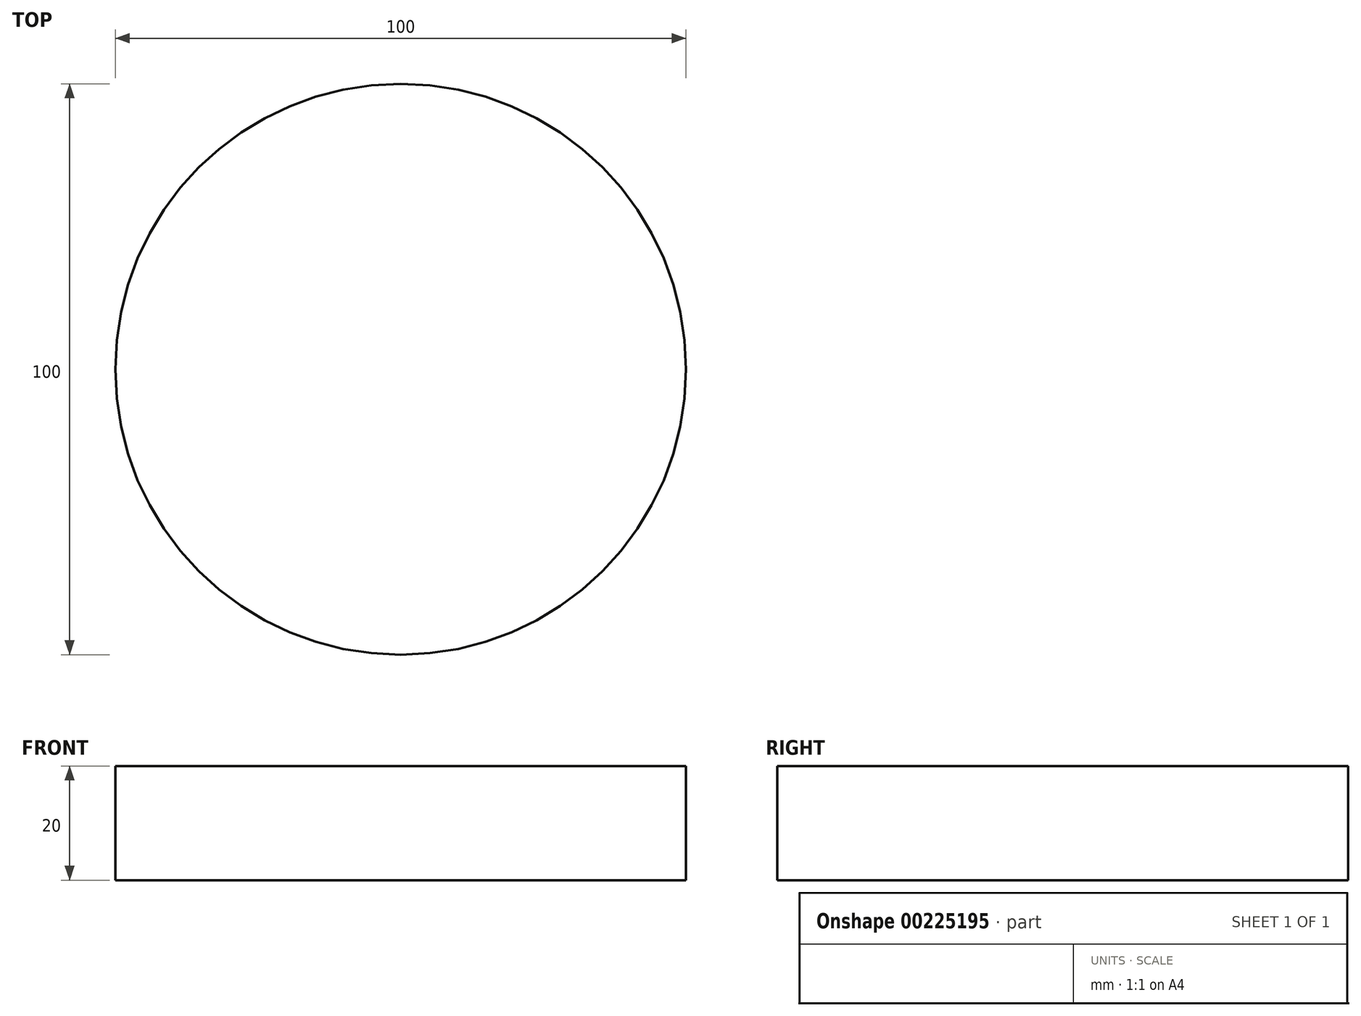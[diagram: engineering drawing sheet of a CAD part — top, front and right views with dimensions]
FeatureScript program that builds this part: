
annotation { "Feature Type Name" : "Feature", "Feature Type Description" : "" }
export const myFeature = defineFeature(function(context is Context, id is Id, definition is map)
    precondition{}
    {
        {
            var Q0;
            Q0=qCreatedBy(makeId("Top.planeOp"),FACE);
            var sketch = newSketch(context, id + "F0", { "sketchPlane" : qUnion([Q0])});
            skCircle(sketch, "E0", {"center": v(0, 0) * mm, "radius": 50 * mm});
            skCircle(sketch, "E1", {"center": v(0, 0) * mm, "radius": 110 * mm});
            skCircle(sketch, "E2", {"center": v(-83.15, 34.45) * mm, "radius": 9 * mm});
            skCircle(sketch, "E3", {"center": v(-83.15, -34.45) * mm, "radius": 9 * mm});
            skCircle(sketch, "E4", {"center": v(83.15, 34.45) * mm, "radius": 9 * mm});
            skCircle(sketch, "E5", {"center": v(83.15, -34.45) * mm, "radius": 9 * mm});
            skCircle(sketch, "E6", {"center": v(-34.45, 83.15) * mm, "radius": 9 * mm});
            skCircle(sketch, "E7", {"center": v(-34.45, -83.15) * mm, "radius": 9 * mm});
            skCircle(sketch, "E8", {"center": v(34.45, 83.15) * mm, "radius": 9 * mm});
            skCircle(sketch, "E9", {"center": v(34.45, -83.15) * mm, "radius": 9 * mm});
            skSolve(sketch);
        }
        {
            var Q0;
            Q0=makeQuery(id+"F0.imprint","IMPRINT",FACE,{"disambiguationData":[TD([[makeQuery(id+"F0.imprint","IMPRINT",EDGE,{"derivedFrom":sQuery(id+"F0.wireOp",EDGE,"E0")}),1.0]])]});
            extrude(context, id + "F1", {"entities" : qUnion([Q0]), "depth" : 20 * mm});
        }
    });
